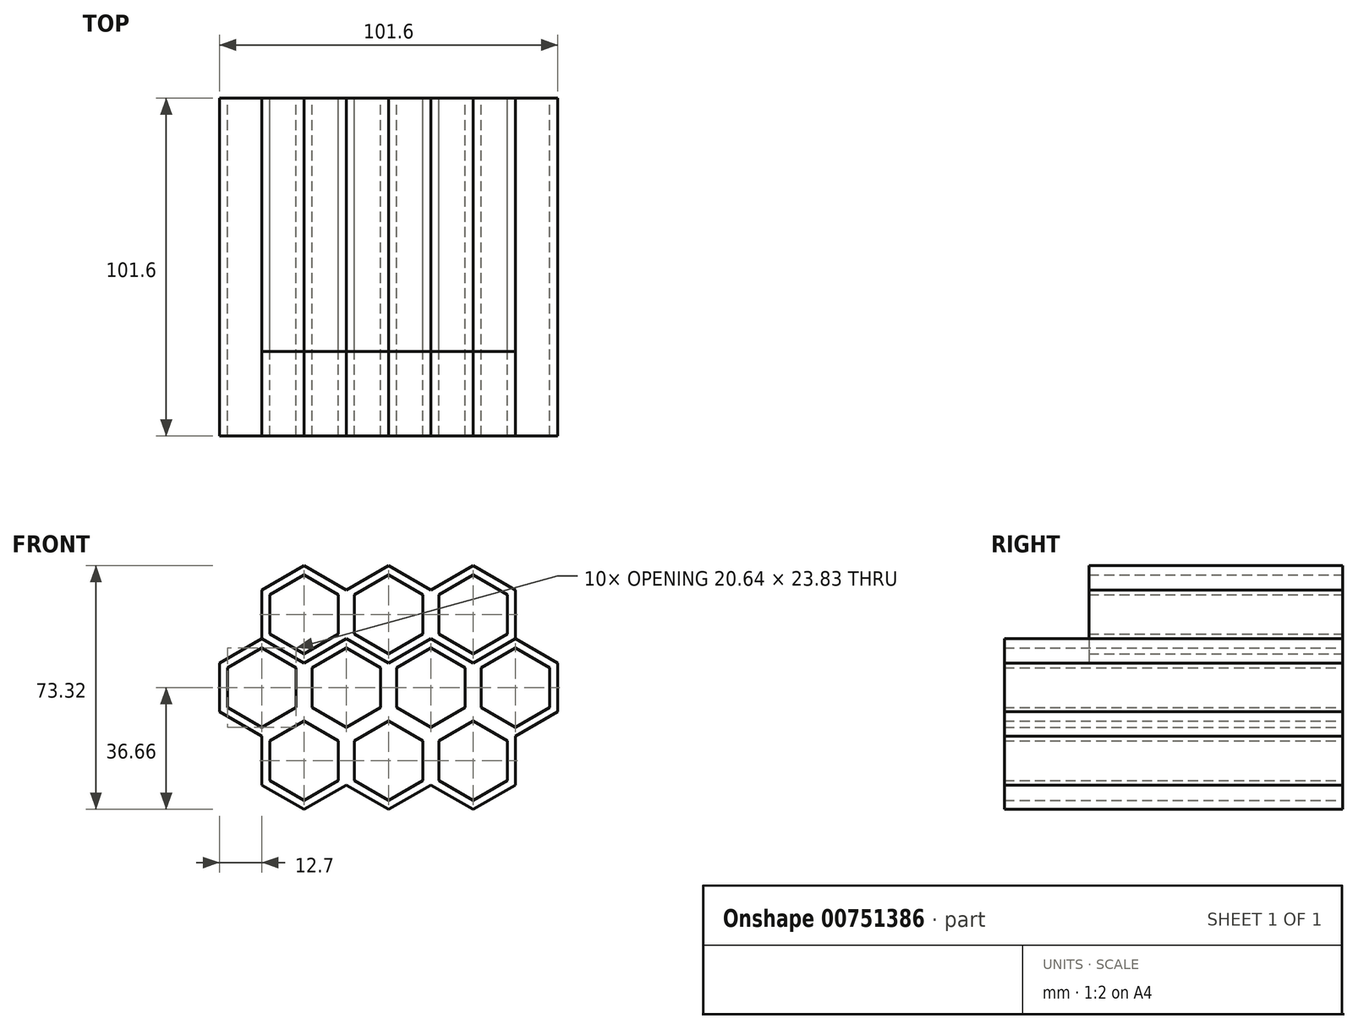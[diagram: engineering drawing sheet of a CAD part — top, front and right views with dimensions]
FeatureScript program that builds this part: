
annotation { "Feature Type Name" : "Feature", "Feature Type Description" : "" }
export const myFeature = defineFeature(function(context is Context, id is Id, definition is map)
    precondition{}
    {
        {
            var Q0;
            Q0=qCreatedBy(makeId("Front.planeOp"),FACE);
            var sketch = newSketch(context, id + "F0", { "sketchPlane" : qUnion([Q0])});
            skPoint(sketch, "E0.0.midPoint", {"position": v(-19.05, 11) * mm});
            skLineSegment(sketch, "E1.MirrorCS", {"start": v(-50.8, 7.33) * mm, "end": v(-50.8, 0) * mm});
            skLineSegment(sketch, "E2.MirrorCS", {"start": v(-38.1, 14.66) * mm, "end": v(-50.8, 7.33) * mm});
            skPoint(sketch, "E3.MirrorP", {"position": v(-31.75, 11) * mm});
            skLineSegment(sketch, "E4.0", {"start": v(-12.7, 29.33) * mm, "end": v(0, 36.66) * mm});
            skLineSegment(sketch, "E4.4", {"start": v(0, 7.33) * mm, "end": v(-12.7, 14.66) * mm});
            skLineSegment(sketch, "E4.5", {"start": v(-12.7, 14.66) * mm, "end": v(-12.7, 29.33) * mm});
            skPoint(sketch, "E4.0.midPoint", {"position": v(-6.35, 33) * mm});
            skLineSegment(sketch, "E5.MirrorCS", {"start": v(-38.1, 14.66) * mm, "end": v(-25.4, 7.33) * mm});
            skLineSegment(sketch, "E6.MirrorCS", {"start": v(-25.4, 7.33) * mm, "end": v(-12.7, 14.66) * mm});
            skLineSegment(sketch, "E7.MirrorCS", {"start": v(-38.1, 29.33) * mm, "end": v(-38.1, 14.66) * mm});
            skLineSegment(sketch, "E8.MirrorCS", {"start": v(-25.4, 36.66) * mm, "end": v(-38.1, 29.33) * mm});
            skLineSegment(sketch, "E9.MirrorCS", {"start": v(-12.7, 29.33) * mm, "end": v(-25.4, 36.66) * mm});
            skPoint(sketch, "E10.MirrorP", {"position": v(-19.05, 33) * mm});
            skLineSegment(sketch, "E11", {"start": v(0, -64.3) * mm, "end": v(0, 49.87) * mm, "construction": true});
            skLineSegment(sketch, "E12", {"start": v(94.5, 0) * mm, "end": v(-92.24, 0) * mm, "construction": true});
            skLineSegment(sketch, "E13.0", {"start": v(-15.08, 16.04) * mm, "end": v(-15.08, 27.95) * mm});
            skLineSegment(sketch, "E13.1", {"start": v(-25.4, 33.91) * mm, "end": v(-35.72, 27.95) * mm});
            skLineSegment(sketch, "E13.2", {"start": v(-35.72, 27.95) * mm, "end": v(-35.72, 16.04) * mm});
            skLineSegment(sketch, "E13.3", {"start": v(-15.08, 27.95) * mm, "end": v(-25.4, 33.91) * mm});
            skLineSegment(sketch, "E13.4", {"start": v(-35.72, 16.04) * mm, "end": v(-25.4, 10.08) * mm});
            skLineSegment(sketch, "E13.5", {"start": v(-25.4, 10.08) * mm, "end": v(-15.08, 16.04) * mm});
            skLineSegment(sketch, "E14.0", {"start": v(-10.32, 27.95) * mm, "end": v(0, 33.91) * mm});
            skLineSegment(sketch, "E14.1", {"start": v(-10.32, 16.04) * mm, "end": v(-10.32, 27.95) * mm});
            skLineSegment(sketch, "E14.2", {"start": v(0, 10.08) * mm, "end": v(-10.32, 16.04) * mm});
            skLineSegment(sketch, "E15.0", {"start": v(-48.42, 5.96) * mm, "end": v(-48.42, 0) * mm});
            skLineSegment(sketch, "E15.1", {"start": v(-38.1, 11.92) * mm, "end": v(-48.42, 5.96) * mm});
            skLineSegment(sketch, "E15.2", {"start": v(-38.1, 11.92) * mm, "end": v(-27.78, 5.96) * mm});
            skLineSegment(sketch, "E15.3", {"start": v(-27.78, 0) * mm, "end": v(-27.78, 5.96) * mm});
            skLineSegment(sketch, "E16.0", {"start": v(-2.38, 5.96) * mm, "end": v(-12.7, 11.92) * mm});
            skLineSegment(sketch, "E16.1", {"start": v(-23.02, 5.96) * mm, "end": v(-12.7, 11.92) * mm});
            skLineSegment(sketch, "E16.2", {"start": v(-23.02, 0) * mm, "end": v(-23.02, 5.96) * mm});
            skLineSegment(sketch, "E17.MirrorCS", {"start": v(-2.38, 0) * mm, "end": v(-2.38, 5.96) * mm});
            skLineSegment(sketch, "E18.MirrorCS", {"start": v(-48.42, -5.96) * mm, "end": v(-48.42, 0) * mm});
            skLineSegment(sketch, "E19.MirrorCS", {"start": v(-50.8, -7.33) * mm, "end": v(-50.8, 0) * mm});
            skLineSegment(sketch, "E20.MirrorCS", {"start": v(-25.4, -33.91) * mm, "end": v(-35.72, -27.95) * mm});
            skLineSegment(sketch, "E21.MirrorCS", {"start": v(-27.78, 0) * mm, "end": v(-27.78, -5.96) * mm});
            skLineSegment(sketch, "E22.MirrorCS", {"start": v(0, -10.08) * mm, "end": v(-10.32, -16.04) * mm});
            skLineSegment(sketch, "E23.MirrorCS", {"start": v(-23.02, 0) * mm, "end": v(-23.02, -5.96) * mm});
            skLineSegment(sketch, "E24.MirrorCS", {"start": v(-25.4, -10.08) * mm, "end": v(-15.08, -16.04) * mm});
            skLineSegment(sketch, "E25.MirrorCS", {"start": v(-12.7, -29.33) * mm, "end": v(0, -36.66) * mm});
            skLineSegment(sketch, "E26.MirrorCS", {"start": v(-25.4, -36.66) * mm, "end": v(-38.1, -29.33) * mm});
            skLineSegment(sketch, "E27.MirrorCS", {"start": v(-35.72, -27.95) * mm, "end": v(-35.72, -16.04) * mm});
            skLineSegment(sketch, "E28.MirrorCS", {"start": v(-15.08, -27.95) * mm, "end": v(-25.4, -33.91) * mm});
            skPoint(sketch, "E29.MirrorP", {"position": v(-19.05, -33) * mm});
            skLineSegment(sketch, "E30.MirrorCS", {"start": v(-10.32, -27.95) * mm, "end": v(0, -33.91) * mm});
            skLineSegment(sketch, "E31.MirrorCS", {"start": v(-35.72, -16.04) * mm, "end": v(-25.4, -10.08) * mm});
            skLineSegment(sketch, "E32.MirrorCS", {"start": v(-38.1, -11.92) * mm, "end": v(-27.78, -5.96) * mm});
            skLineSegment(sketch, "E33.MirrorCS", {"start": v(-15.08, -16.04) * mm, "end": v(-15.08, -27.95) * mm});
            skLineSegment(sketch, "E34.MirrorCS", {"start": v(-38.1, -14.66) * mm, "end": v(-50.8, -7.33) * mm});
            skLineSegment(sketch, "E35.MirrorCS", {"start": v(-38.1, -29.33) * mm, "end": v(-38.1, -14.66) * mm});
            skLineSegment(sketch, "E36.MirrorCS", {"start": v(-23.02, -5.96) * mm, "end": v(-12.7, -11.92) * mm});
            skLineSegment(sketch, "E37.MirrorCS", {"start": v(-2.38, 0) * mm, "end": v(-2.38, -5.96) * mm});
            skLineSegment(sketch, "E38.MirrorCS", {"start": v(-38.1, -11.92) * mm, "end": v(-48.42, -5.96) * mm});
            skLineSegment(sketch, "E39.MirrorCS", {"start": v(-12.7, -29.33) * mm, "end": v(-25.4, -36.66) * mm});
            skPoint(sketch, "E40.MirrorP", {"position": v(-6.35, -33) * mm});
            skLineSegment(sketch, "E41.MirrorCS", {"start": v(-2.38, -5.96) * mm, "end": v(-12.7, -11.92) * mm});
            skLineSegment(sketch, "E42.MirrorCS", {"start": v(-10.32, -16.04) * mm, "end": v(-10.32, -27.95) * mm});
            skLineSegment(sketch, "E43.MirrorCS", {"start": v(48.42, -5.96) * mm, "end": v(48.42, 0) * mm});
            skLineSegment(sketch, "E44.MirrorCS", {"start": v(23.02, 0) * mm, "end": v(23.02, -5.96) * mm});
            skLineSegment(sketch, "E45.MirrorCS", {"start": v(27.78, 0) * mm, "end": v(27.78, -5.96) * mm});
            skLineSegment(sketch, "E46.MirrorCS", {"start": v(2.38, 0) * mm, "end": v(2.38, -5.96) * mm});
            skLineSegment(sketch, "E47.MirrorCS", {"start": v(15.08, 27.95) * mm, "end": v(25.4, 33.91) * mm});
            skLineSegment(sketch, "E48.MirrorCS", {"start": v(38.1, 14.66) * mm, "end": v(25.4, 7.33) * mm});
            skLineSegment(sketch, "E49.MirrorCS", {"start": v(12.7, 29.33) * mm, "end": v(25.4, 36.66) * mm});
            skLineSegment(sketch, "E50.MirrorCS", {"start": v(23.02, 5.96) * mm, "end": v(12.7, 11.92) * mm});
            skLineSegment(sketch, "E51.MirrorCS", {"start": v(48.42, 5.96) * mm, "end": v(48.42, 0) * mm});
            skLineSegment(sketch, "E52.MirrorCS", {"start": v(12.7, -29.33) * mm, "end": v(0, -36.66) * mm});
            skLineSegment(sketch, "E53.MirrorCS", {"start": v(10.32, 27.95) * mm, "end": v(0, 33.91) * mm});
            skLineSegment(sketch, "E54.MirrorCS", {"start": v(12.7, 29.33) * mm, "end": v(0, 36.66) * mm});
            skLineSegment(sketch, "E55.MirrorCS", {"start": v(38.1, 11.92) * mm, "end": v(27.78, 5.96) * mm});
            skLineSegment(sketch, "E56.MirrorCS", {"start": v(50.8, 7.33) * mm, "end": v(50.8, 0) * mm});
            skLineSegment(sketch, "E57.MirrorCS", {"start": v(25.4, 7.33) * mm, "end": v(12.7, 14.66) * mm});
            skLineSegment(sketch, "E58.MirrorCS", {"start": v(12.7, -29.33) * mm, "end": v(25.4, -36.66) * mm});
            skLineSegment(sketch, "E59.MirrorCS", {"start": v(35.72, -16.04) * mm, "end": v(25.4, -10.08) * mm});
            skLineSegment(sketch, "E60.MirrorCS", {"start": v(25.4, -10.08) * mm, "end": v(15.08, -16.04) * mm});
            skPoint(sketch, "E61.MirrorP", {"position": v(19.05, -33) * mm});
            skPoint(sketch, "E62.MirrorP", {"position": v(19.05, 11) * mm});
            skLineSegment(sketch, "E63.MirrorCS", {"start": v(25.4, 36.66) * mm, "end": v(38.1, 29.33) * mm});
            skPoint(sketch, "E64.MirrorP", {"position": v(19.05, 33) * mm});
            skLineSegment(sketch, "E65.MirrorCS", {"start": v(15.08, -16.04) * mm, "end": v(15.08, -27.95) * mm});
            skLineSegment(sketch, "E66.MirrorCS", {"start": v(38.1, 14.66) * mm, "end": v(50.8, 7.33) * mm});
            skLineSegment(sketch, "E67.MirrorCS", {"start": v(38.1, 11.92) * mm, "end": v(48.42, 5.96) * mm});
            skLineSegment(sketch, "E68.MirrorCS", {"start": v(10.32, -16.04) * mm, "end": v(10.32, -27.95) * mm});
            skLineSegment(sketch, "E69.MirrorCS", {"start": v(35.72, 27.95) * mm, "end": v(35.72, 16.04) * mm});
            skLineSegment(sketch, "E70.MirrorCS", {"start": v(2.38, -5.96) * mm, "end": v(12.7, -11.92) * mm});
            skLineSegment(sketch, "E71.MirrorCS", {"start": v(2.38, 0) * mm, "end": v(2.38, 5.96) * mm});
            skLineSegment(sketch, "E72.MirrorCS", {"start": v(38.1, -14.66) * mm, "end": v(50.8, -7.33) * mm});
            skLineSegment(sketch, "E73.MirrorCS", {"start": v(0, -10.08) * mm, "end": v(10.32, -16.04) * mm});
            skLineSegment(sketch, "E74.MirrorCS", {"start": v(10.32, 16.04) * mm, "end": v(10.32, 27.95) * mm});
            skLineSegment(sketch, "E75.MirrorCS", {"start": v(23.02, -5.96) * mm, "end": v(12.7, -11.92) * mm});
            skLineSegment(sketch, "E76.MirrorCS", {"start": v(50.8, -7.33) * mm, "end": v(50.8, 0) * mm});
            skLineSegment(sketch, "E77.MirrorCS", {"start": v(0, 10.08) * mm, "end": v(10.32, 16.04) * mm});
            skPoint(sketch, "E78.MirrorP", {"position": v(6.35, 33) * mm});
            skLineSegment(sketch, "E79.MirrorCS", {"start": v(23.02, 0) * mm, "end": v(23.02, 5.96) * mm});
            skLineSegment(sketch, "E80.MirrorCS", {"start": v(15.08, -27.95) * mm, "end": v(25.4, -33.91) * mm});
            skLineSegment(sketch, "E81.MirrorCS", {"start": v(25.4, 33.91) * mm, "end": v(35.72, 27.95) * mm});
            skLineSegment(sketch, "E82.MirrorCS", {"start": v(27.78, 0) * mm, "end": v(27.78, 5.96) * mm});
            skLineSegment(sketch, "E83.MirrorCS", {"start": v(15.08, 16.04) * mm, "end": v(15.08, 27.95) * mm});
            skLineSegment(sketch, "E84.MirrorCS", {"start": v(10.32, -27.95) * mm, "end": v(0, -33.91) * mm});
            skLineSegment(sketch, "E85.MirrorCS", {"start": v(2.38, 5.96) * mm, "end": v(12.7, 11.92) * mm});
            skLineSegment(sketch, "E86.MirrorCS", {"start": v(25.4, 10.08) * mm, "end": v(15.08, 16.04) * mm});
            skLineSegment(sketch, "E87.MirrorCS", {"start": v(35.72, -27.95) * mm, "end": v(35.72, -16.04) * mm});
            skLineSegment(sketch, "E88.MirrorCS", {"start": v(25.4, -33.91) * mm, "end": v(35.72, -27.95) * mm});
            skLineSegment(sketch, "E89.MirrorCS", {"start": v(38.1, -11.92) * mm, "end": v(27.78, -5.96) * mm});
            skPoint(sketch, "E90.MirrorP", {"position": v(31.75, 11) * mm});
            skLineSegment(sketch, "E91.MirrorCS", {"start": v(38.1, 29.33) * mm, "end": v(38.1, 14.66) * mm});
            skLineSegment(sketch, "E92.MirrorCS", {"start": v(38.1, -29.33) * mm, "end": v(38.1, -14.66) * mm});
            skLineSegment(sketch, "E93.MirrorCS", {"start": v(35.72, 16.04) * mm, "end": v(25.4, 10.08) * mm});
            skLineSegment(sketch, "E94.MirrorCS", {"start": v(38.1, -11.92) * mm, "end": v(48.42, -5.96) * mm});
            skLineSegment(sketch, "E95.MirrorCS", {"start": v(0, 7.33) * mm, "end": v(12.7, 14.66) * mm});
            skLineSegment(sketch, "E96.MirrorCS", {"start": v(25.4, -36.66) * mm, "end": v(38.1, -29.33) * mm});
            skLineSegment(sketch, "E97.MirrorCS", {"start": v(12.7, 14.66) * mm, "end": v(12.7, 29.33) * mm});
            skPoint(sketch, "E98.MirrorP", {"position": v(6.35, -33) * mm});
            skSolve(sketch);
        }
        {
            var Q0;
            Q0=makeQuery(id+"F0.imprint","IMPRINT",FACE,{"disambiguationData":[TD([[makeQuery(id+"F0.imprint","IMPRINT",EDGE,{"derivedFrom":sQuery(id+"F0.wireOp",EDGE,"E1.MirrorCS")}),1.0]])]});
            extrude(context, id + "F1", {"entities" : qUnion([Q0]), "depth" : 101.6 * mm, "offsetDistance" : 25.4 * mm});
        }
        {
            var Q0;
            Q0=makeQuery(id+"F0.imprint","IMPRINT",FACE,{"disambiguationData":[TD([[makeQuery(id+"F0.imprint","IMPRINT",EDGE,{"derivedFrom":sQuery(id+"F0.wireOp",EDGE,"E4.5")}),1.0]])]});
            var Q1;
            Q1=makeQuery(id+"F0.imprint","IMPRINT",FACE,{"disambiguationData":[TD([[makeQuery(id+"F0.imprint","IMPRINT",EDGE,{"derivedFrom":sQuery(id+"F0.wireOp",EDGE,"E4.0")}),-1.0]])]});
            var Q2;
            Q2=makeQuery(id+"F0.imprint","IMPRINT",FACE,{"disambiguationData":[TD([[makeQuery(id+"F0.imprint","IMPRINT",EDGE,{"derivedFrom":sQuery(id+"F0.wireOp",EDGE,"E47.MirrorCS")}),1.0]])]});
            extrude(context, id + "F2", {"entities" : qUnion([Q0, Q1, Q2]), "operationType" : NewBodyOperationType.ADD, "depth" : 76.2 * mm, "offsetDistance" : 25.4 * mm});
        }
    });
